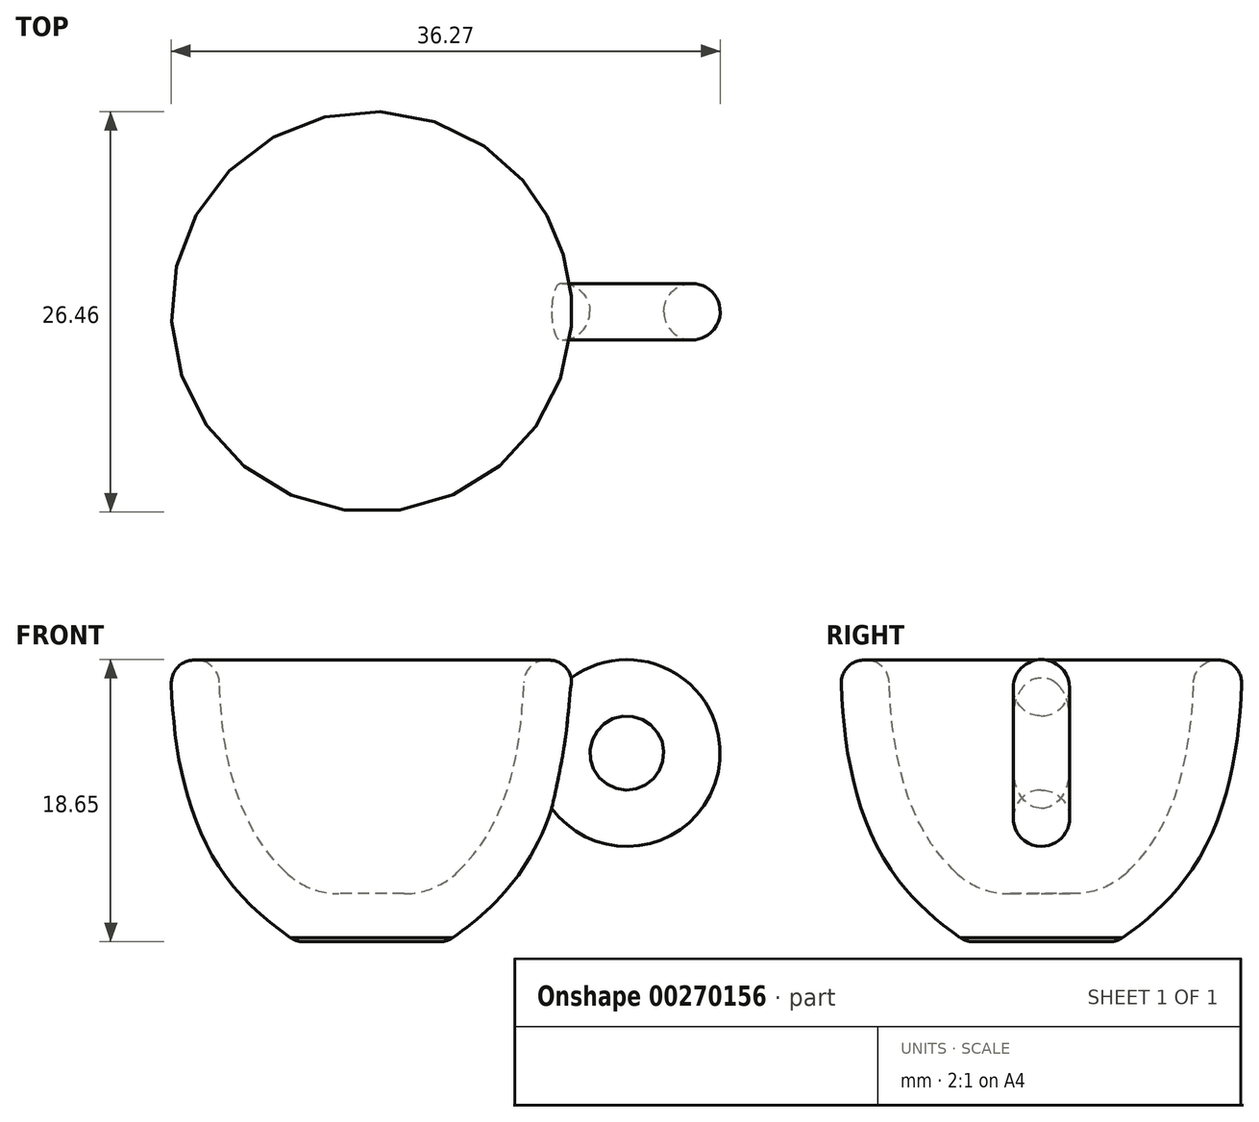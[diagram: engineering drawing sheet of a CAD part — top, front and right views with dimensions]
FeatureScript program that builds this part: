
annotation { "Feature Type Name" : "Feature", "Feature Type Description" : "" }
export const myFeature = defineFeature(function(context is Context, id is Id, definition is map)
    precondition{}
    {
        {
            var Q0;
            Q0=qCreatedBy(makeId("Front.planeOp"),FACE);
            var sketch = newSketch(context, id + "F0", { "sketchPlane" : qUnion([Q0])});
            skLineSegment(sketch, "E0", {"start": v(0, 80.6) * mm, "end": v(0, -81.49) * mm, "construction": true});
            skLineSegment(sketch, "E1", {"start": v(0, 0) * mm, "end": v(4.97, 0) * mm});
            skFitSpline(sketch, "E2", {"points": [v(4.97, 0) * mm, v(13.26, 18.61) * mm], "startDerivative": vector(11.52, 7.92) * mm, "endDerivative": vector(0, 36.4) * mm});
            skLineSegment(sketch, "E3", {"start": v(13.26, 18.61) * mm, "end": v(0, 18.61) * mm});
            skLineSegment(sketch, "E4", {"start": v(0, 18.61) * mm, "end": v(0, 0) * mm});
            skSolve(sketch);
        }
        {
            var Q0;
            Q0 = qSketchRegion(id + "F0", true);
            var Q1;
            Q1=sQuery(id+"F0.wireOp",EDGE,"E0");
            revolve(context, id + "F1", {"entities" : qUnion([Q0]), "axis" : qUnion([Q1]), "revolveType" : RevolveType.FULL});
        }
        {
            var Q0;
            Q0=makeQuery(id+"F1.opRevolve","SWEPT_FACE",FACE,{"disambiguationData":[OSD([sQuery(id+"F0.wireOp",EDGE,"E3")])]});
            shell(context, id + "F2", {"entities" : qUnion([Q0]), "thickness" : 3.17 * mm});
        }
        {
            var Q0;
            Q0=makeQuery(id+"F1.opRevolve","SWEPT_EDGE",EDGE,{"disambiguationData":[OSD([sQuery(id+"F0.wireOp",EDGE,"E2"),sQuery(id+"F0.wireOp",EDGE,"E3")])]});
            var Q1;
            Q1=makeQuery(id+"F2.opShell","OFFSET_EDGE",EDGE,{"disambiguationData":[OSD([sQuery(id+"F0.wireOp",EDGE,"E2"),sQuery(id+"F0.wireOp",EDGE,"E3")])]});
            var Q2;
            Q2=makeQuery(id+"F1.opRevolve","SWEPT_FACE",FACE,{"disambiguationData":[OSD([sQuery(id+"F0.wireOp",EDGE,"E1")])]});
            fillet(context, id + "F3", {"entities" : qUnion([Q0, Q1, Q2]), "radius" : 1.52 * mm, "tangentPropagation" : true, "allowEdgeOverflow" : false});
        }
        {
            var Q0;
            Q0=qCreatedBy(makeId("Front.planeOp"),FACE);
            var sketch = newSketch(context, id + "F4", { "sketchPlane" : qUnion([Q0])});
            skCircle(sketch, "E5", {"center": v(16.87, 12.48) * mm, "radius": 5.17 * mm});
            skLineSegment(sketch, "E6", {"start": v(24.05, 12.48) * mm, "end": v(9.19, 12.48) * mm, "construction": true});
            skSolve(sketch);
        }
        {
            var Q0;
            Q0=sQuery(id+"F4.wireOp",EDGE,"E6");
            var Q1;
            Q1=qCreatedBy(makeId("Top.planeOp"),FACE);
            cPlane(context, id + "F5", {"entities" : qUnion([Q0, Q1]), "cplaneType" : CPlaneType.LINE_ANGLE, "offset" : 25.4 * mm, "angle" : 0 * degree, "width" : 152.4 * mm, "height" : 152.4 * mm});
        }
        {
            var Q0;
            Q0=qCreatedBy(id+"F5.planeOp",FACE);
            var sketch = newSketch(context, id + "F6", { "sketchPlane" : qUnion([Q0])});
            skCircle(sketch, "E7", {"center": v(21.18, 0) * mm, "radius": 1.86 * mm});
            skLineSegment(sketch, "E8", {"start": v(24.83, 0) * mm, "end": v(14.16, 0) * mm, "construction": true});
            skSolve(sketch);
        }
        {
            var Q0;
            Q0=makeQuery(id+"F6.imprint","IMPRINT",FACE,{"disambiguationData":[TD([[makeQuery(id+"F6.imprint","IMPRINT",EDGE,{"derivedFrom":sQuery(id+"F6.wireOp",EDGE,"E7")}),1.0]])]});
            var Q1;
            Q1=sQuery(id+"F4.wireOp",EDGE,"E5");
            sweep(context, id + "F7", {"operationType" : NewBodyOperationType.ADD, "profiles" : qUnion([Q0]), "path" : qUnion([Q1])});
        }
        {
            var Q0;
            Q0=makeQuery(id+"F2.opShell","OFFSET_EDGE",EDGE,{"disambiguationData":[OSD([sQuery(id+"F0.wireOp",EDGE,"E1"),sQuery(id+"F0.wireOp",EDGE,"E2")])]});
            fillet(context, id + "F8", {"entities" : qUnion([Q0]), "radius" : 5.08 * mm, "tangentPropagation" : true, "allowEdgeOverflow" : false});
        }
    });
